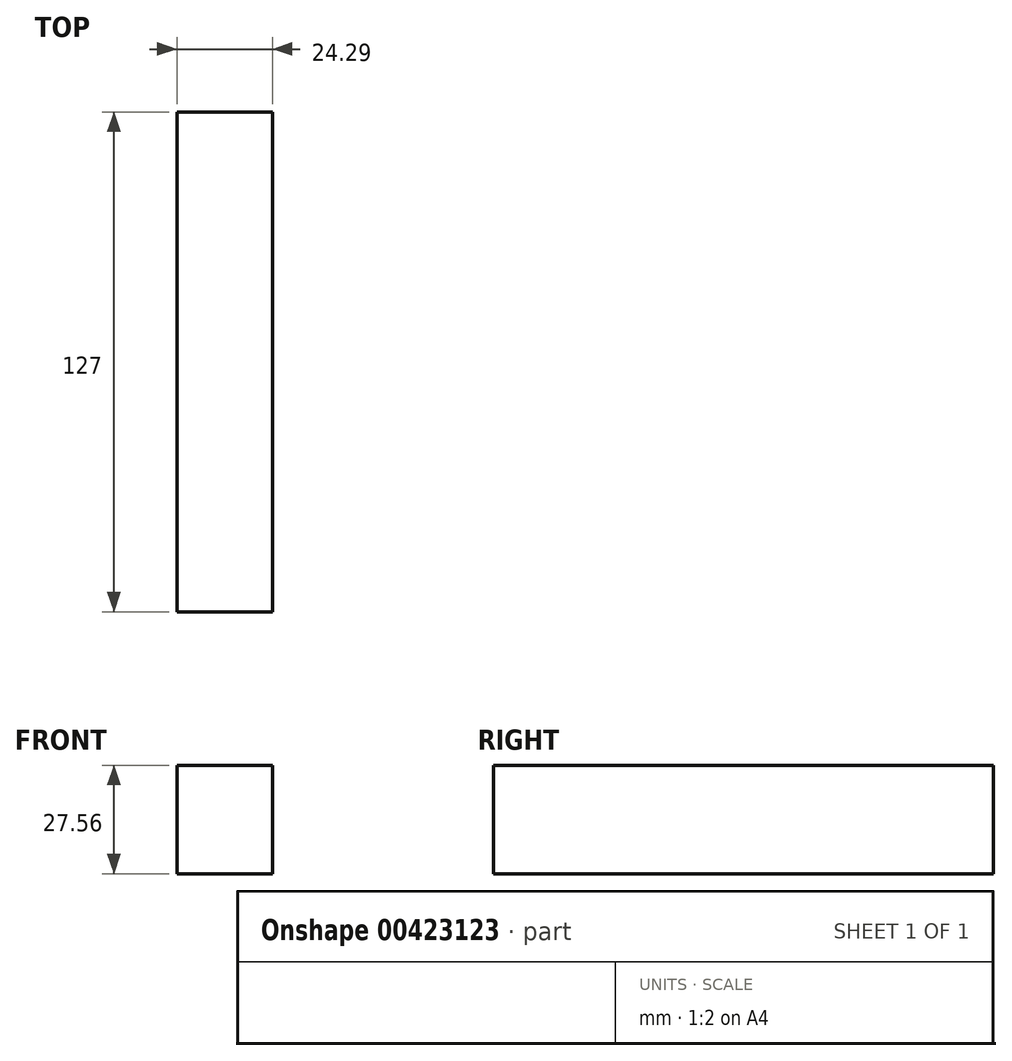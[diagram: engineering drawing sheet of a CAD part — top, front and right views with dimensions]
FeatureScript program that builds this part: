
annotation { "Feature Type Name" : "Feature", "Feature Type Description" : "" }
export const myFeature = defineFeature(function(context is Context, id is Id, definition is map)
    precondition{}
    {
        {
            var Q0;
            Q0=qCreatedBy(makeId("Front.planeOp"),FACE);
            var sketch = newSketch(context, id + "F0", { "sketchPlane" : qUnion([Q0])});
            skLineSegment(sketch, "E0.bottom", {"start": v(0, 0) * mm, "end": v(24.29, 0) * mm});
            skLineSegment(sketch, "E0.top", {"start": v(0, 27.56) * mm, "end": v(24.29, 27.56) * mm});
            skLineSegment(sketch, "E0.left", {"start": v(0, 0) * mm, "end": v(0, 27.56) * mm});
            skLineSegment(sketch, "E0.right", {"start": v(24.29, 0) * mm, "end": v(24.29, 27.56) * mm});
            skSolve(sketch);
        }
        {
            var Q0;
            Q0=makeQuery(id+"F0.imprint","IMPRINT",FACE,{"disambiguationData":[TD([[makeQuery(id+"F0.imprint","IMPRINT",EDGE,{"derivedFrom":sQuery(id+"F0.wireOp",EDGE,"E0.bottom")}),1.0]])]});
            extrude(context, id + "F1", {"entities" : qUnion([Q0]), "depth" : 127 * mm});
        }
    });
